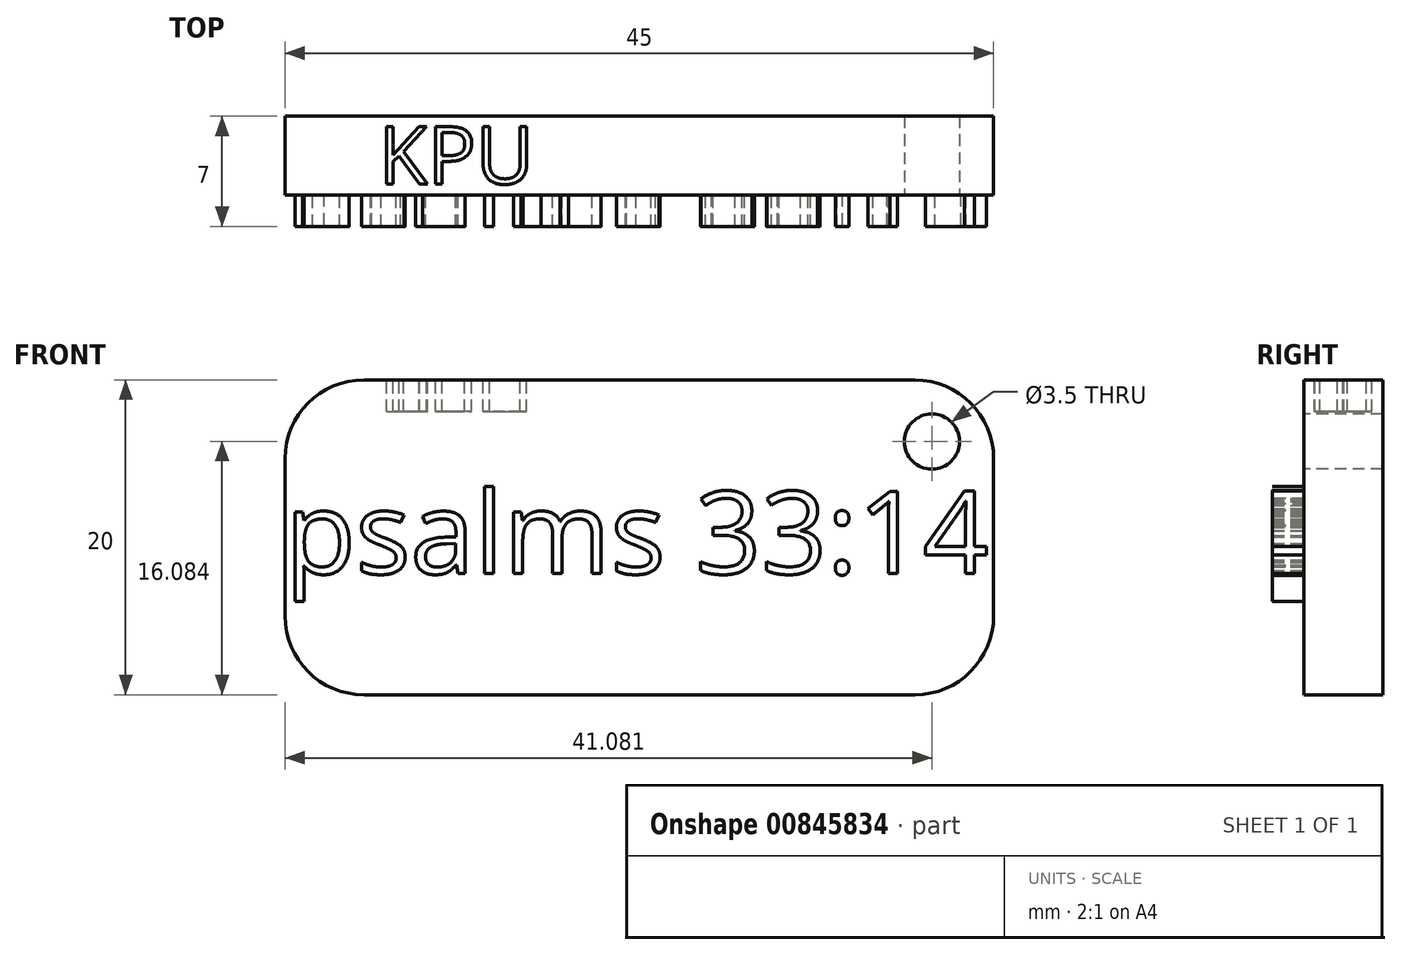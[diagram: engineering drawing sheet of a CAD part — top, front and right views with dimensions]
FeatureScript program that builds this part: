
annotation { "Feature Type Name" : "Feature", "Feature Type Description" : "" }
export const myFeature = defineFeature(function(context is Context, id is Id, definition is map)
    precondition{}
    {
        {
            var Q0;
            Q0=qCreatedBy(makeId("Front.planeOp"),FACE);
            var sketch = newSketch(context, id + "F0", { "sketchPlane" : qUnion([Q0])});
            skLineSegment(sketch, "E0.bottom", {"start": v(0, 0) * mm, "end": v(45, 0) * mm});
            skLineSegment(sketch, "E0.top", {"start": v(0, 20) * mm, "end": v(45, 20) * mm});
            skLineSegment(sketch, "E0.left", {"start": v(0, 0) * mm, "end": v(0, 20) * mm});
            skLineSegment(sketch, "E0.right", {"start": v(45, 0) * mm, "end": v(45, 20) * mm});
            skSolve(sketch);
        }
        {
            var Q0;
            Q0=makeQuery(id+"F0.imprint","IMPRINT",FACE,{"disambiguationData":[TD([[makeQuery(id+"F0.imprint","IMPRINT",EDGE,{"derivedFrom":sQuery(id+"F0.wireOp",EDGE,"E0.bottom")}),1.0]])]});
            extrude(context, id + "F1", {"entities" : qUnion([Q0]), "depth" : 5 * mm, "offsetDistance" : 25 * mm});
        }
        {
            var Q0;
            Q0=makeQuery(id+"F1.opExtrude","CAP_FACE",FACE,{"disambiguationData":[OSD([sQuery(id+"F0.wireOp",EDGE,"E0.bottom"),sQuery(id+"F0.wireOp",EDGE,"E0.top"),sQuery(id+"F0.wireOp",EDGE,"E0.left"),sQuery(id+"F0.wireOp",EDGE,"E0.right")])],"isStart":false});
            var sketch = newSketch(context, id + "F2", { "sketchPlane" : qUnion([Q0])});
            skText(sketch, "E1", { "text": "psalms 33:14", "fontName": "OpenSans-Regular.ttf"});
            const initialGuessF2  = {"E1": [0, 0.00769, 1, 0, 0.00526]};
            skSetInitialGuess(sketch, initialGuessF2);
            skSolve(sketch);
        }
        {
            var Q0;
            Q0 = qSketchRegion(id + "F2", true);
            extrude(context, id + "F3", {"entities" : qUnion([Q0]), "operationType" : NewBodyOperationType.ADD, "depth" : 2 * mm, "offsetDistance" : 25 * mm});
        }
        {
            var Q0;
            Q0=makeQuery(id+"F1.opExtrude","SWEPT_EDGE",EDGE,{"disambiguationData":[OSD([sQuery(id+"F0.wireOp",EDGE,"E0.top"),sQuery(id+"F0.wireOp",EDGE,"E0.left")])]});
            var Q1;
            Q1=makeQuery(id+"F1.opExtrude","SWEPT_EDGE",EDGE,{"disambiguationData":[OSD([sQuery(id+"F0.wireOp",EDGE,"E0.top"),sQuery(id+"F0.wireOp",EDGE,"E0.right")])]});
            var Q2;
            Q2=makeQuery(id+"F1.opExtrude","SWEPT_EDGE",EDGE,{"disambiguationData":[OSD([sQuery(id+"F0.wireOp",EDGE,"E0.bottom"),sQuery(id+"F0.wireOp",EDGE,"E0.right")])]});
            var Q3;
            Q3=makeQuery(id+"F1.opExtrude","SWEPT_EDGE",EDGE,{"disambiguationData":[OSD([sQuery(id+"F0.wireOp",EDGE,"E0.bottom"),sQuery(id+"F0.wireOp",EDGE,"E0.left")])]});
            fillet(context, id + "F4", {"entities" : qUnion([Q0, Q1, Q2, Q3]), "radius" : 5 * mm, "tangentPropagation" : true, "allowEdgeOverflow" : false});
        }
        {
            var Q0;
            Q0=makeQuery(id+"F1.opExtrude","SWEPT_FACE",FACE,{"disambiguationData":[OSD([sQuery(id+"F0.wireOp",EDGE,"E0.top")])]});
            var sketch = newSketch(context, id + "F5", { "sketchPlane" : qUnion([Q0])});
            skText(sketch, "E2", { "text": "KPU", "fontName": "OpenSans-Regular.ttf"});
            const initialGuessF5  = {"E2": [0.00593, -0.0043, 1, 0, 0.00366]};
            skSetInitialGuess(sketch, initialGuessF5);
            skSolve(sketch);
        }
        {
            var Q0;
            Q0 = qSketchRegion(id + "F5", true);
            extrude(context, id + "F6", {"entities" : qUnion([Q0]), "operationType" : NewBodyOperationType.REMOVE, "oppositeDirection" : true, "depth" : 2 * mm, "offsetDistance" : 25 * mm});
        }
        {
            var Q0;
            {var subQ0=sQuery(id+"F0.wireOp",EDGE,"E0.left");var subQ1=sQuery(id+"F0.wireOp",EDGE,"E0.bottom");var subQ2=sQuery(id+"F0.wireOp",EDGE,"E0.right");var subQ3=sQuery(id+"F0.wireOp",EDGE,"E0.top");Q0=makeQuery(id+"F3.boolean.opBoolean","SPLIT",FACE,{"disambiguationData":[TD([makeQuery(id+"F1.opExtrude","SWEPT_FACE",FACE,{"disambiguationData":[OSD([subQ1])]})])],"derivedFrom":makeQuery(id+"F1.opExtrude","CAP_FACE",FACE,{"disambiguationData":[OSD([subQ1,subQ3,subQ0,subQ2])],"isStart":false})});}
            var sketch = newSketch(context, id + "F7", { "sketchPlane" : qUnion([Q0])});
            skCircle(sketch, "E3", {"center": v(41.08, 16.08) * mm, "radius": 1.75 * mm});
            skSolve(sketch);
        }
        {
            var Q0;
            Q0=makeQuery(id+"F7.imprint","IMPRINT",FACE,{"disambiguationData":[TD([[makeQuery(id+"F7.imprint","IMPRINT",EDGE,{"derivedFrom":sQuery(id+"F7.wireOp",EDGE,"E3")}),1.0]])]});
            extrude(context, id + "F8", {"entities" : qUnion([Q0]), "operationType" : NewBodyOperationType.REMOVE, "oppositeDirection" : true, "depth" : 5 * mm, "offsetDistance" : 25 * mm});
        }
    });
